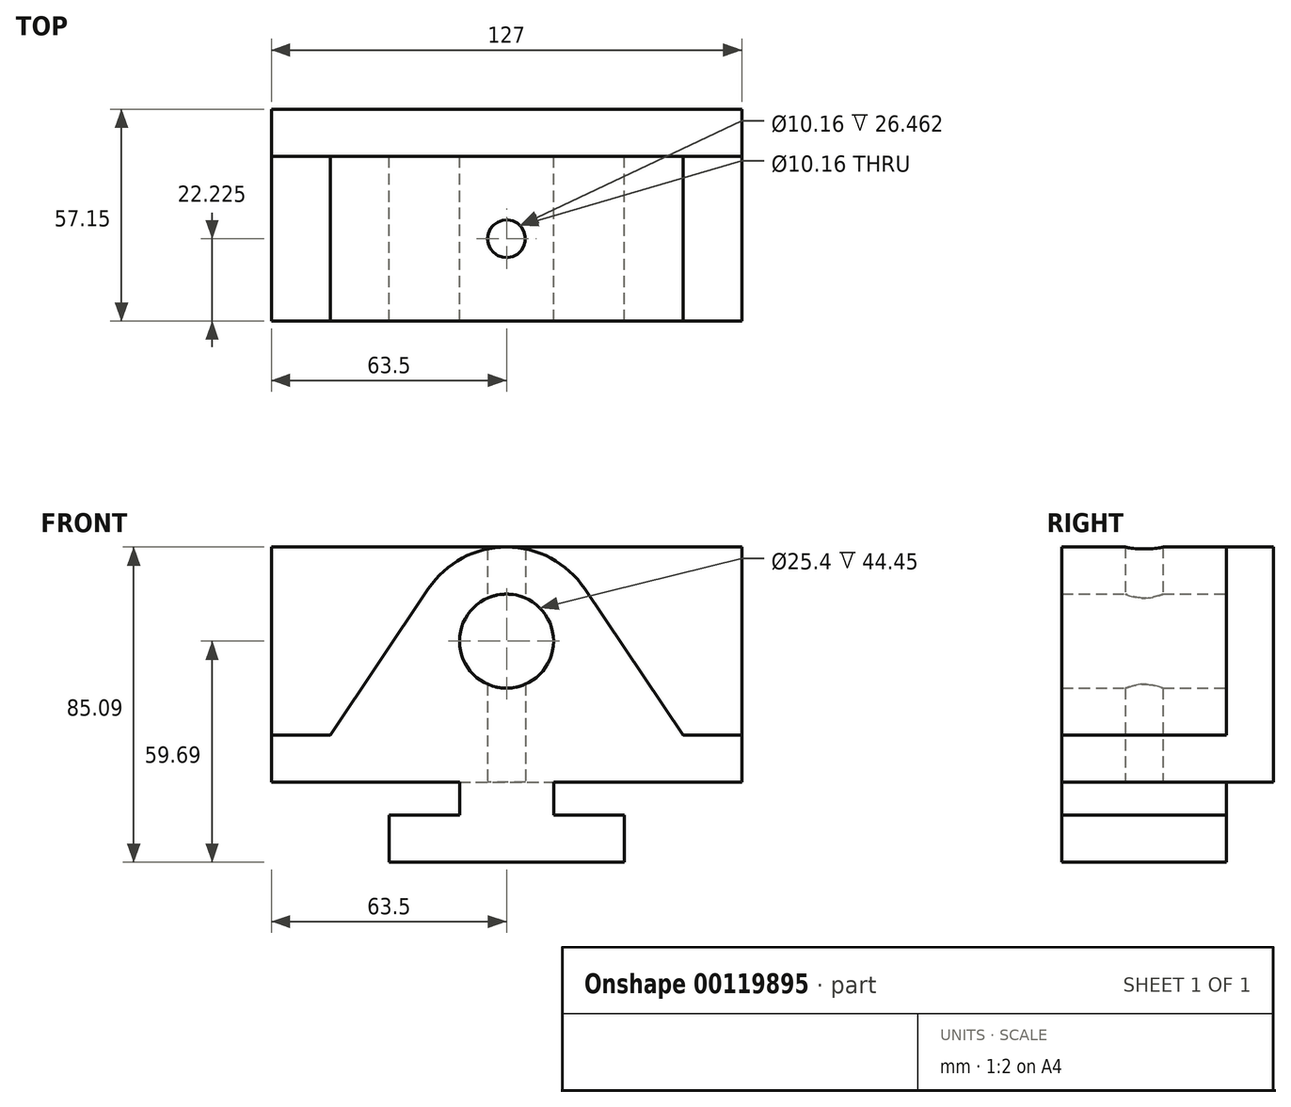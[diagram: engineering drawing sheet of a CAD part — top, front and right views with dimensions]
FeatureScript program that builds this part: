
annotation { "Feature Type Name" : "Feature", "Feature Type Description" : "" }
export const myFeature = defineFeature(function(context is Context, id is Id, definition is map)
    precondition{}
    {
        {
            var Q0;
            Q0=qCreatedBy(makeId("Front.planeOp"),FACE);
            var sketch = newSketch(context, id + "F0", { "sketchPlane" : qUnion([Q0])});
            skLineSegment(sketch, "E0", {"start": v(-31.75, -21.59) * mm, "end": v(0, -21.59) * mm});
            skLineSegment(sketch, "E1", {"start": v(31.75, -21.6) * mm, "end": v(31.75, -8.9) * mm});
            skLineSegment(sketch, "E2", {"start": v(31.75, -8.9) * mm, "end": v(12.7, -8.9) * mm});
            skLineSegment(sketch, "E3", {"start": v(12.7, -8.9) * mm, "end": v(12.7, 0) * mm});
            skLineSegment(sketch, "E4", {"start": v(12.7, 0) * mm, "end": v(63.5, 0) * mm});
            skLineSegment(sketch, "E5", {"start": v(63.5, 0) * mm, "end": v(63.5, 12.7) * mm});
            skLineSegment(sketch, "E6", {"start": v(63.5, 12.7) * mm, "end": v(47.62, 12.7) * mm});
            skLineSegment(sketch, "E7", {"start": v(47.63, 12.7) * mm, "end": v(21.1, 52.25) * mm});
            skLineSegment(sketch, "E8", {"start": v(-31.75, -21.6) * mm, "end": v(-31.75, -8.9) * mm});
            skLineSegment(sketch, "E9", {"start": v(-31.75, -8.9) * mm, "end": v(-12.7, -8.9) * mm});
            skLineSegment(sketch, "E10", {"start": v(-12.7, -8.9) * mm, "end": v(-12.7, 0) * mm});
            skLineSegment(sketch, "E11", {"start": v(-12.7, 0) * mm, "end": v(-63.5, 0) * mm});
            skLineSegment(sketch, "E12", {"start": v(-63.5, 0) * mm, "end": v(-63.5, 12.7) * mm});
            skLineSegment(sketch, "E13", {"start": v(-63.5, 12.7) * mm, "end": v(-63.5, 12.7) * mm});
            skLineSegment(sketch, "E14", {"start": v(-47.63, 12.7) * mm, "end": v(-63.5, 12.7) * mm});
            skPoint(sketch, "E15.start.orphan", {"position": v(0, -21.6) * mm});
            skLineSegment(sketch, "E16", {"start": v(31.75, -21.59) * mm, "end": v(0, -21.59) * mm});
            skLineSegment(sketch, "E17", {"start": v(0, -21.59) * mm, "end": v(0, 62.73) * mm, "construction": true});
            skPoint(sketch, "E18", {"position": v(0, 0) * mm});
            skPoint(sketch, "E19.positionSnap0", {"position": v(0, 12.7) * mm});
            skLineSegment(sketch, "E20", {"start": v(-47.63, 12.7) * mm, "end": v(-21.1, 52.25) * mm});
            skArc(sketch, "E21", {"start": v(-21.1, 52.25) * mm, "mid": v(0, 63.5) * mm, "end": v(21.1, 52.25) * mm});
            skPoint(sketch, "E22.positionSnap0", {"position": v(0, 63.5) * mm});
            skCircle(sketch, "E23", {"center": v(0, 38.1) * mm, "radius": 12.7 * mm});
            skSolve(sketch);
        }
        {
            var Q0;
            Q0 = qSketchRegion(id + "F0", true);
            extrude(context, id + "F1", {"entities" : qUnion([Q0]), "depth" : 44.45 * mm});
        }
        {
            var Q0;
            Q0=qCreatedBy(makeId("Front.planeOp"),FACE);
            var sketch = newSketch(context, id + "F2", { "sketchPlane" : qUnion([Q0])});
            skLineSegment(sketch, "E24.0", {"start": v(-63.5, 0) * mm, "end": v(-63.5, 63.5) * mm});
            skLineSegment(sketch, "E25.0", {"start": v(-12.7, 0) * mm, "end": v(-63.5, 0) * mm});
            skLineSegment(sketch, "E26.0", {"start": v(12.7, 0) * mm, "end": v(63.5, 0) * mm});
            skLineSegment(sketch, "E27.0", {"start": v(63.5, 0) * mm, "end": v(63.5, 63.5) * mm});
            skLineSegment(sketch, "E28", {"start": v(-63.5, 63.5) * mm, "end": v(63.5, 63.5) * mm});
            skPoint(sketch, "E29", {"position": v(0, 63.5) * mm});
            skLineSegment(sketch, "E30", {"start": v(12.7, 0) * mm, "end": v(-12.7, 0) * mm});
            skSolve(sketch);
        }
        {
            var Q0;
            Q0 = qSketchRegion(id + "F2", true);
            extrude(context, id + "F3", {"entities" : qUnion([Q0]), "operationType" : NewBodyOperationType.ADD, "oppositeDirection" : true, "depth" : 12.7 * mm});
        }
        {
            var Q0;
            Q0=qCreatedBy(makeId("Top.planeOp"),FACE);
            var sketch = newSketch(context, id + "F4", { "sketchPlane" : qUnion([Q0])});
            skCircle(sketch, "E31", {"center": v(0, -22.23) * mm, "radius": 5.08 * mm});
            skSolve(sketch);
        }
        {
            var Q0;
            Q0 = qSketchRegion(id + "F4", true);
            var Q1;
            Q1=sQuery(id+"F4.wireOp",EDGE,"E31");
            var Q2;
            Q2=makeQuery(id+"F1.opExtrude","SWEPT_BODY",BODY,{"disambiguationData":[OSD([sQuery(id+"F0.wireOp",EDGE,"E0"),sQuery(id+"F0.wireOp",EDGE,"E1"),sQuery(id+"F0.wireOp",EDGE,"E2"),sQuery(id+"F0.wireOp",EDGE,"E3"),sQuery(id+"F0.wireOp",EDGE,"E4"),sQuery(id+"F0.wireOp",EDGE,"E5"),sQuery(id+"F0.wireOp",EDGE,"E6"),sQuery(id+"F0.wireOp",EDGE,"E7"),sQuery(id+"F0.wireOp",EDGE,"E8"),sQuery(id+"F0.wireOp",EDGE,"E9"),sQuery(id+"F0.wireOp",EDGE,"E10"),sQuery(id+"F0.wireOp",EDGE,"E11"),sQuery(id+"F0.wireOp",EDGE,"E12"),sQuery(id+"F0.wireOp",EDGE,"E14"),sQuery(id+"F0.wireOp",EDGE,"E16"),sQuery(id+"F0.wireOp",EDGE,"E20"),sQuery(id+"F0.wireOp",EDGE,"E21"),sQuery(id+"F0.wireOp",EDGE,"E23")])]});
            extrude(context, id + "F5", {"entities" : qUnion([Q0]), "operationType" : NewBodyOperationType.REMOVE, "surfaceEntities" : qUnion([Q1]), "endBound" : BoundingType.THROUGH_ALL, "endBoundEntityBody" : qUnion([Q2]), "depth" : 25.4 * mm});
        }
    });
